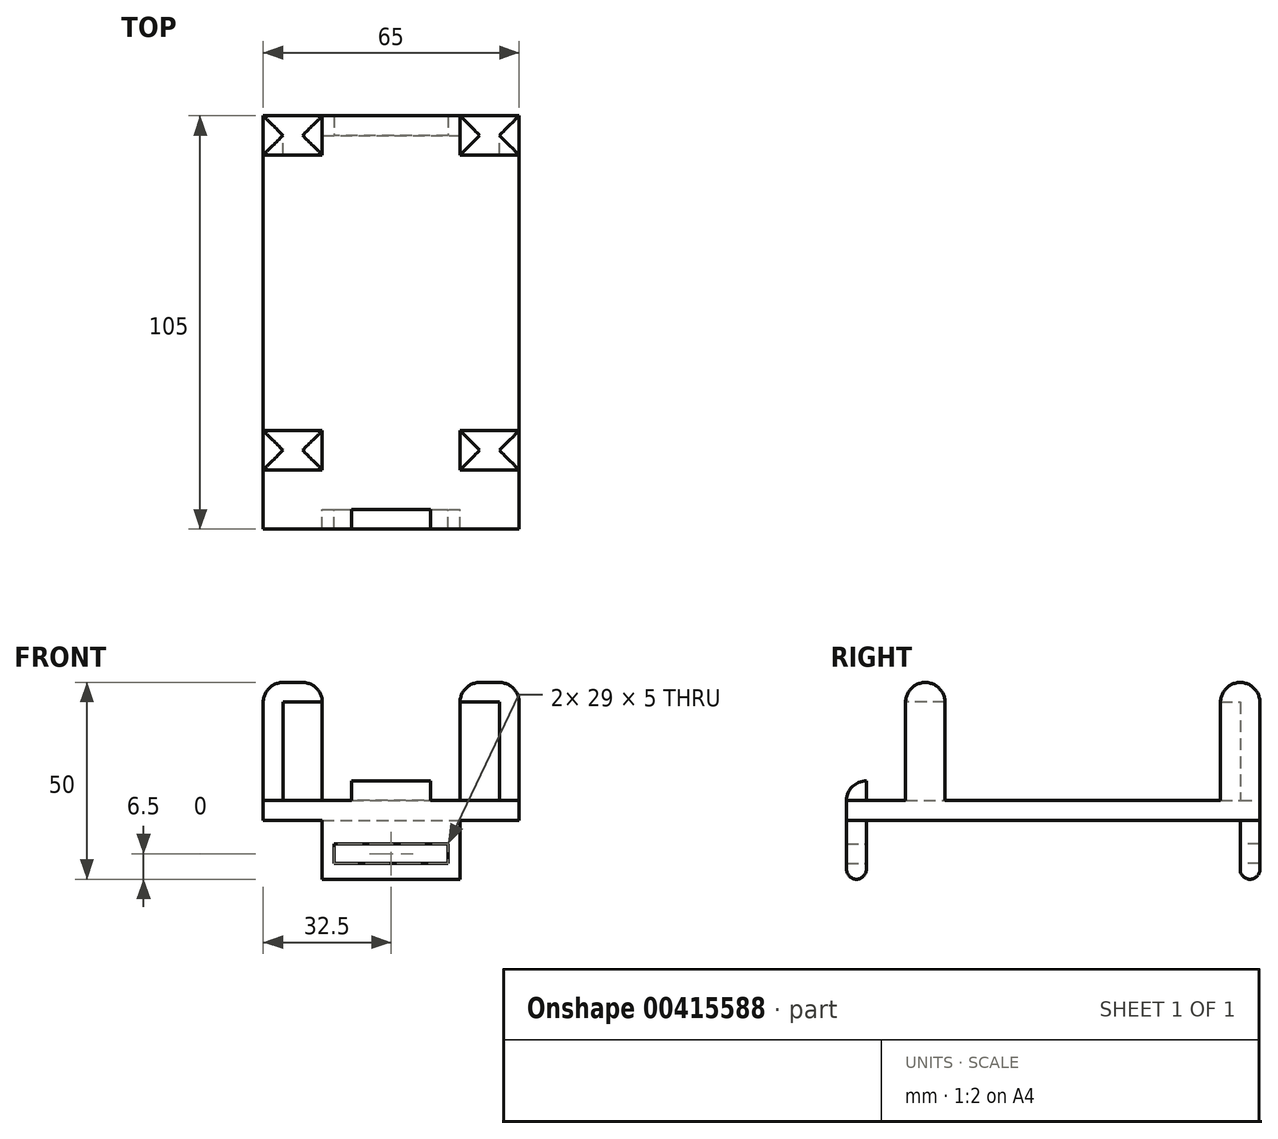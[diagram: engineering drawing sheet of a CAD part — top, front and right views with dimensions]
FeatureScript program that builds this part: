
annotation { "Feature Type Name" : "Feature", "Feature Type Description" : "" }
export const myFeature = defineFeature(function(context is Context, id is Id, definition is map)
    precondition{}
    {
        {
            var Q0;
            Q0=qCreatedBy(makeId("Top.planeOp"),FACE);
            var sketch = newSketch(context, id + "F0", { "sketchPlane" : qUnion([Q0])});
            skLineSegment(sketch, "E0.bottom", {"start": v(32.5, 52.5) * mm, "end": v(-32.5, 52.5) * mm});
            skLineSegment(sketch, "E0.top", {"start": v(32.5, -52.5) * mm, "end": v(-32.5, -52.5) * mm});
            skLineSegment(sketch, "E0.left", {"start": v(32.5, 52.5) * mm, "end": v(32.5, -52.5) * mm});
            skLineSegment(sketch, "E0.right", {"start": v(-32.5, 52.5) * mm, "end": v(-32.5, -52.5) * mm});
            skPoint(sketch, "E0.middle", {"position": v(0, 0) * mm});
            skSolve(sketch);
        }
        {
            var Q0;
            Q0=makeQuery(id+"F0.imprint","IMPRINT",FACE,{"disambiguationData":[TD([[makeQuery(id+"F0.imprint","IMPRINT",EDGE,{"derivedFrom":sQuery(id+"F0.wireOp",EDGE,"E0.bottom")}),1.0]])]});
            var sketch = newSketch(context, id + "F1", { "sketchPlane" : qUnion([Q0])});
            skLineSegment(sketch, "E1.bottom", {"start": v(-27.5, 52.5) * mm, "end": v(-22.5, 52.5) * mm});
            skLineSegment(sketch, "E1.top", {"start": v(-27.5, 47.5) * mm, "end": v(-22.5, 47.5) * mm});
            skLineSegment(sketch, "E1.right", {"start": v(-22.5, 52.5) * mm, "end": v(-22.5, 47.5) * mm});
            skLineSegment(sketch, "E2.MirrorCS", {"start": v(22.5, 52.5) * mm, "end": v(22.5, 47.5) * mm});
            skLineSegment(sketch, "E3.MirrorCS", {"start": v(27.5, 52.5) * mm, "end": v(22.5, 52.5) * mm});
            skLineSegment(sketch, "E4.MirrorCS", {"start": v(27.5, 47.5) * mm, "end": v(22.5, 47.5) * mm});
            skLineSegment(sketch, "E5.top", {"start": v(-27.5, 42.5) * mm, "end": v(-32.5, 42.5) * mm});
            skLineSegment(sketch, "E5.left", {"start": v(-27.5, 47.5) * mm, "end": v(-27.5, 42.5) * mm});
            skLineSegment(sketch, "E5.right", {"start": v(-32.5, 47.5) * mm, "end": v(-32.5, 42.5) * mm});
            skLineSegment(sketch, "E6.MirrorCS", {"start": v(27.5, 47.5) * mm, "end": v(27.5, 42.5) * mm});
            skLineSegment(sketch, "E7.MirrorCS", {"start": v(27.5, 42.5) * mm, "end": v(32.5, 42.5) * mm});
            skLineSegment(sketch, "E8", {"start": v(-32.5, 47.5) * mm, "end": v(-32.5, 52.5) * mm});
            skLineSegment(sketch, "E9", {"start": v(-32.5, 52.5) * mm, "end": v(-27.5, 52.5) * mm});
            skLineSegment(sketch, "E10", {"start": v(32.5, 42.5) * mm, "end": v(32.5, 52.5) * mm});
            skLineSegment(sketch, "E11", {"start": v(32.5, 52.5) * mm, "end": v(27.5, 52.5) * mm});
            skSolve(sketch);
        }
        {
            var Q0;
            Q0=makeQuery(id+"F0.imprint","IMPRINT",FACE,{"disambiguationData":[TD([[makeQuery(id+"F0.imprint","IMPRINT",EDGE,{"derivedFrom":sQuery(id+"F0.wireOp",EDGE,"E0.bottom")}),1.0]])]});
            extrude(context, id + "F2", {"entities" : qUnion([Q0]), "depth" : 5 * mm});
        }
        {
            var Q0;
            Q0=makeQuery(id+"F1.imprint","IMPRINT",FACE,{"disambiguationData":[TD([[makeQuery(id+"F1.imprint","IMPRINT",EDGE,{"derivedFrom":sQuery(id+"F1.wireOp",EDGE,"E1.bottom")}),1.0]])]});
            var Q1;
            Q1=makeQuery(id+"F1.imprint","IMPRINT",FACE,{"disambiguationData":[TD([[makeQuery(id+"F1.imprint","IMPRINT",EDGE,{"derivedFrom":sQuery(id+"F1.wireOp",EDGE,"E2.MirrorCS")}),1.0]])]});
            extrude(context, id + "F3", {"entities" : qUnion([Q0, Q1]), "operationType" : NewBodyOperationType.ADD, "depth" : 35 * mm});
        }
        {
            var Q0;
            Q0=makeQuery(id+"F3.opExtrude","SWEPT_FACE",FACE,{"disambiguationData":[OSD([sQuery(id+"F1.wireOp",EDGE,"E6.MirrorCS")])]});
            var sketch = newSketch(context, id + "F4", { "sketchPlane" : qUnion([Q0])});
            skLineSegment(sketch, "E12.bottom", {"start": v(-42.5, 35) * mm, "end": v(-47.5, 35) * mm});
            skLineSegment(sketch, "E12.top", {"start": v(-42.5, 30) * mm, "end": v(-47.5, 30) * mm});
            skLineSegment(sketch, "E12.left", {"start": v(-42.5, 35) * mm, "end": v(-42.5, 30) * mm});
            skLineSegment(sketch, "E12.right", {"start": v(-47.5, 35) * mm, "end": v(-47.5, 30) * mm});
            skSolve(sketch);
        }
        {
            var Q0;
            Q0=makeQuery(id+"F4.imprint","IMPRINT",FACE,{"disambiguationData":[TD([[makeQuery(id+"F4.imprint","IMPRINT",EDGE,{"derivedFrom":sQuery(id+"F4.wireOp",EDGE,"E12.bottom")}),-1.0]])]});
            extrude(context, id + "F5", {"entities" : qUnion([Q0]), "operationType" : NewBodyOperationType.ADD, "depth" : 5 * mm});
        }
        {
            var Q0;
            Q0=makeQuery(id+"F3.opExtrude","SWEPT_FACE",FACE,{"disambiguationData":[OSD([sQuery(id+"F1.wireOp",EDGE,"E5.left")])]});
            var sketch = newSketch(context, id + "F6", { "sketchPlane" : qUnion([Q0])});
            skLineSegment(sketch, "E13.bottom", {"start": v(42.5, 35) * mm, "end": v(47.5, 35) * mm});
            skLineSegment(sketch, "E13.top", {"start": v(42.5, 30) * mm, "end": v(47.5, 30) * mm});
            skLineSegment(sketch, "E13.left", {"start": v(42.5, 35) * mm, "end": v(42.5, 30) * mm});
            skLineSegment(sketch, "E13.right", {"start": v(47.5, 35) * mm, "end": v(47.5, 30) * mm});
            skSolve(sketch);
        }
        {
            var Q0;
            Q0=makeQuery(id+"F6.imprint","IMPRINT",FACE,{"disambiguationData":[TD([[makeQuery(id+"F6.imprint","IMPRINT",EDGE,{"derivedFrom":sQuery(id+"F6.wireOp",EDGE,"E13.bottom")}),1.0]])]});
            extrude(context, id + "F7", {"entities" : qUnion([Q0]), "operationType" : NewBodyOperationType.ADD, "depth" : 5 * mm});
        }
        {
            var Q0;
            Q0=makeQuery(id+"F2.opExtrude","CAP_FACE",FACE,{"disambiguationData":[OSD([sQuery(id+"F0.wireOp",EDGE,"E0.bottom"),sQuery(id+"F0.wireOp",EDGE,"E0.top"),sQuery(id+"F0.wireOp",EDGE,"E0.left"),sQuery(id+"F0.wireOp",EDGE,"E0.right")])],"isStart":false});
            var sketch = newSketch(context, id + "F8", { "sketchPlane" : qUnion([Q0])});
            skLineSegment(sketch, "E14.bottom", {"start": v(-32.5, -37.5) * mm, "end": v(-27.5, -37.5) * mm});
            skLineSegment(sketch, "E14.top", {"start": v(-32.5, -27.5) * mm, "end": v(-27.5, -27.5) * mm});
            skLineSegment(sketch, "E14.left", {"start": v(-32.5, -37.5) * mm, "end": v(-32.5, -27.5) * mm});
            skLineSegment(sketch, "E14.right", {"start": v(-27.5, -37.5) * mm, "end": v(-27.5, -27.5) * mm});
            skLineSegment(sketch, "E15.MirrorCS", {"start": v(27.5, -37.5) * mm, "end": v(27.5, -27.5) * mm});
            skLineSegment(sketch, "E16.MirrorCS", {"start": v(32.5, -27.5) * mm, "end": v(27.5, -27.5) * mm});
            skLineSegment(sketch, "E17.MirrorCS", {"start": v(32.5, -37.5) * mm, "end": v(27.5, -37.5) * mm});
            skLineSegment(sketch, "E18.MirrorCS", {"start": v(32.5, -37.5) * mm, "end": v(32.5, -27.5) * mm});
            skSolve(sketch);
        }
        {
            var Q0;
            Q0=makeQuery(id+"F8.imprint","IMPRINT",FACE,{"disambiguationData":[TD([[makeQuery(id+"F8.imprint","IMPRINT",EDGE,{"derivedFrom":sQuery(id+"F8.wireOp",EDGE,"E15.MirrorCS")}),-1.0]])]});
            var Q1;
            Q1=makeQuery(id+"F8.imprint","IMPRINT",FACE,{"disambiguationData":[TD([[makeQuery(id+"F8.imprint","IMPRINT",EDGE,{"derivedFrom":sQuery(id+"F8.wireOp",EDGE,"E14.bottom")}),1.0]])]});
            extrude(context, id + "F9", {"entities" : qUnion([Q0, Q1]), "operationType" : NewBodyOperationType.ADD, "depth" : 30 * mm});
        }
        {
            var Q0;
            Q0=makeQuery(id+"F9.opExtrude","SWEPT_FACE",FACE,{"disambiguationData":[OSD([sQuery(id+"F8.wireOp",EDGE,"E14.right")])]});
            var sketch = newSketch(context, id + "F10", { "sketchPlane" : qUnion([Q0])});
            skLineSegment(sketch, "E19.bottom", {"start": v(-27.5, 35) * mm, "end": v(-37.5, 35) * mm});
            skLineSegment(sketch, "E19.top", {"start": v(-27.5, 30) * mm, "end": v(-37.5, 30) * mm});
            skLineSegment(sketch, "E19.left", {"start": v(-27.5, 35) * mm, "end": v(-27.5, 30) * mm});
            skLineSegment(sketch, "E19.right", {"start": v(-37.5, 35) * mm, "end": v(-37.5, 30) * mm});
            skSolve(sketch);
        }
        {
            var Q0;
            Q0=makeQuery(id+"F9.opExtrude","SWEPT_FACE",FACE,{"disambiguationData":[OSD([sQuery(id+"F8.wireOp",EDGE,"E15.MirrorCS")])]});
            var sketch = newSketch(context, id + "F11", { "sketchPlane" : qUnion([Q0])});
            skLineSegment(sketch, "E20.bottom", {"start": v(27.5, 35) * mm, "end": v(37.5, 35) * mm});
            skLineSegment(sketch, "E20.top", {"start": v(27.5, 30) * mm, "end": v(37.5, 30) * mm});
            skLineSegment(sketch, "E20.left", {"start": v(27.5, 35) * mm, "end": v(27.5, 30) * mm});
            skLineSegment(sketch, "E20.right", {"start": v(37.5, 35) * mm, "end": v(37.5, 30) * mm});
            skSolve(sketch);
        }
        {
            var Q0;
            Q0 = qSketchRegion(id + "F11", true);
            extrude(context, id + "F12", {"entities" : qUnion([Q0]), "operationType" : NewBodyOperationType.ADD, "depth" : 10 * mm});
        }
        {
            var Q0;
            Q0=makeQuery(id+"F10.imprint","IMPRINT",FACE,{"disambiguationData":[TD([[makeQuery(id+"F10.imprint","IMPRINT",EDGE,{"derivedFrom":sQuery(id+"F10.wireOp",EDGE,"E19.bottom")}),-1.0]])]});
            extrude(context, id + "F13", {"entities" : qUnion([Q0]), "operationType" : NewBodyOperationType.ADD, "depth" : 10 * mm});
        }
        {
            var Q0;
            Q0=makeQuery(id+"F5.boolean.opBoolean","MERGE",FACE,{"derivedFrom":[makeQuery(id+"F3.opExtrude","SWEPT_FACE",FACE,{"disambiguationData":[OSD([sQuery(id+"F1.wireOp",EDGE,"E2.MirrorCS")])]}),makeQuery(id+"F5.opExtrude","CAP_FACE",FACE,{"disambiguationData":[OSD([sQuery(id+"F4.wireOp",EDGE,"E12.bottom"),sQuery(id+"F4.wireOp",EDGE,"E12.top"),sQuery(id+"F4.wireOp",EDGE,"E12.left"),sQuery(id+"F4.wireOp",EDGE,"E12.right")])],"isStart":false})]});
            extrude(context, id + "F14", {"entities" : qUnion([Q0]), "operationType" : NewBodyOperationType.ADD, "depth" : 5 * mm});
        }
        {
            var Q0;
            Q0=makeQuery(id+"F7.boolean.opBoolean","MERGE",FACE,{"derivedFrom":[makeQuery(id+"F3.opExtrude","SWEPT_FACE",FACE,{"disambiguationData":[OSD([sQuery(id+"F1.wireOp",EDGE,"E1.right")])]}),makeQuery(id+"F7.opExtrude","CAP_FACE",FACE,{"disambiguationData":[OSD([sQuery(id+"F6.wireOp",EDGE,"E13.bottom"),sQuery(id+"F6.wireOp",EDGE,"E13.top"),sQuery(id+"F6.wireOp",EDGE,"E13.left"),sQuery(id+"F6.wireOp",EDGE,"E13.right")])],"isStart":false})]});
            extrude(context, id + "F15", {"entities" : qUnion([Q0]), "operationType" : NewBodyOperationType.ADD, "depth" : 5 * mm});
        }
        {
            var Q0;
            Q0=makeQuery(id+"F2.opExtrude","CAP_FACE",FACE,{"disambiguationData":[OSD([sQuery(id+"F0.wireOp",EDGE,"E0.bottom"),sQuery(id+"F0.wireOp",EDGE,"E0.top"),sQuery(id+"F0.wireOp",EDGE,"E0.left"),sQuery(id+"F0.wireOp",EDGE,"E0.right")])],"isStart":false});
            var sketch = newSketch(context, id + "F16", { "sketchPlane" : qUnion([Q0])});
            skLineSegment(sketch, "E21.bottom", {"start": v(-10, -52.5) * mm, "end": v(10, -52.5) * mm});
            skLineSegment(sketch, "E21.top", {"start": v(-10, -47.5) * mm, "end": v(10, -47.5) * mm});
            skLineSegment(sketch, "E21.left", {"start": v(-10, -52.5) * mm, "end": v(-10, -47.5) * mm});
            skLineSegment(sketch, "E21.right", {"start": v(10, -52.5) * mm, "end": v(10, -47.5) * mm});
            skSolve(sketch);
        }
        {
            var Q0;
            Q0=makeQuery(id+"F16.imprint","IMPRINT",FACE,{"disambiguationData":[TD([[makeQuery(id+"F16.imprint","IMPRINT",EDGE,{"derivedFrom":sQuery(id+"F16.wireOp",EDGE,"E21.bottom")}),-1.0]])]});
            extrude(context, id + "F17", {"entities" : qUnion([Q0]), "operationType" : NewBodyOperationType.ADD, "depth" : 5 * mm});
        }
        {
            var Q0;
            Q0=makeQuery(id+"F2.opExtrude","CAP_FACE",FACE,{"disambiguationData":[OSD([sQuery(id+"F0.wireOp",EDGE,"E0.bottom"),sQuery(id+"F0.wireOp",EDGE,"E0.top"),sQuery(id+"F0.wireOp",EDGE,"E0.left"),sQuery(id+"F0.wireOp",EDGE,"E0.right")])],"isStart":true});
            var sketch = newSketch(context, id + "F18", { "sketchPlane" : qUnion([Q0])});
            skLineSegment(sketch, "E22.bottom", {"start": v(-17.5, 52.5) * mm, "end": v(17.5, 52.5) * mm});
            skLineSegment(sketch, "E22.top", {"start": v(-17.5, 47.5) * mm, "end": v(17.5, 47.5) * mm});
            skLineSegment(sketch, "E22.left", {"start": v(-17.5, 52.5) * mm, "end": v(-17.5, 47.5) * mm});
            skLineSegment(sketch, "E22.right", {"start": v(17.5, 52.5) * mm, "end": v(17.5, 47.5) * mm});
            skLineSegment(sketch, "E23.MirrorCS", {"start": v(-17.5, -47.5) * mm, "end": v(17.5, -47.5) * mm});
            skLineSegment(sketch, "E24.MirrorCS", {"start": v(-17.5, -52.5) * mm, "end": v(17.5, -52.5) * mm});
            skLineSegment(sketch, "E25.MirrorCS", {"start": v(17.5, -52.5) * mm, "end": v(17.5, -47.5) * mm});
            skLineSegment(sketch, "E26.MirrorCS", {"start": v(-17.5, -52.5) * mm, "end": v(-17.5, -47.5) * mm});
            skSolve(sketch);
        }
        {
            var Q0;
            Q0 = qSketchRegion(id + "F18", true);
            extrude(context, id + "F19", {"entities" : qUnion([Q0]), "operationType" : NewBodyOperationType.ADD, "depth" : 15 * mm});
        }
        {
            var Q0;
            Q0=makeQuery(id+"F19.opExtrude","SWEPT_FACE",FACE,{"disambiguationData":[OSD([sQuery(id+"F18.wireOp",EDGE,"E22.top")])]});
            var sketch = newSketch(context, id + "F20", { "sketchPlane" : qUnion([Q0])});
            skLineSegment(sketch, "E27.bottom", {"start": v(14.5, -11) * mm, "end": v(-14.5, -11) * mm});
            skLineSegment(sketch, "E27.top", {"start": v(14.5, -6) * mm, "end": v(-14.5, -6) * mm});
            skLineSegment(sketch, "E27.left", {"start": v(14.5, -11) * mm, "end": v(14.5, -6) * mm});
            skLineSegment(sketch, "E27.right", {"start": v(-14.5, -11) * mm, "end": v(-14.5, -6) * mm});
            skSolve(sketch);
        }
        {
            var Q0;
            Q0=makeQuery(id+"F19.opExtrude","SWEPT_FACE",FACE,{"disambiguationData":[OSD([sQuery(id+"F18.wireOp",EDGE,"E23.MirrorCS")])]});
            var sketch = newSketch(context, id + "F21", { "sketchPlane" : qUnion([Q0])});
            skLineSegment(sketch, "E28.bottom", {"start": v(14.5, -11) * mm, "end": v(-14.5, -11) * mm});
            skLineSegment(sketch, "E28.top", {"start": v(14.5, -6) * mm, "end": v(-14.5, -6) * mm});
            skLineSegment(sketch, "E28.left", {"start": v(14.5, -11) * mm, "end": v(14.5, -6) * mm});
            skLineSegment(sketch, "E28.right", {"start": v(-14.5, -11) * mm, "end": v(-14.5, -6) * mm});
            skSolve(sketch);
        }
        {
            var Q0;
            Q0=makeQuery(id+"F21.imprint","IMPRINT",FACE,{"disambiguationData":[TD([[makeQuery(id+"F21.imprint","IMPRINT",EDGE,{"derivedFrom":sQuery(id+"F21.wireOp",EDGE,"E28.bottom")}),-1.0]])]});
            extrude(context, id + "F22", {"entities" : qUnion([Q0]), "operationType" : NewBodyOperationType.REMOVE, "oppositeDirection" : true, "depth" : 25 * mm});
        }
        {
            var Q0;
            Q0=makeQuery(id+"F20.imprint","IMPRINT",FACE,{"disambiguationData":[TD([[makeQuery(id+"F20.imprint","IMPRINT",EDGE,{"derivedFrom":sQuery(id+"F20.wireOp",EDGE,"E27.bottom")}),-1.0]])]});
            extrude(context, id + "F23", {"entities" : qUnion([Q0]), "operationType" : NewBodyOperationType.REMOVE, "oppositeDirection" : true, "depth" : 25 * mm});
        }
        {
            var Q0;
            Q0=makeQuery(id+"F19.opExtrude","CAP_EDGE",EDGE,{"disambiguationData":[OSD([sQuery(id+"F18.wireOp",EDGE,"E24.MirrorCS")])],"isStart":false});
            var Q1;
            Q1=makeQuery(id+"F19.opExtrude","CAP_EDGE",EDGE,{"disambiguationData":[OSD([sQuery(id+"F18.wireOp",EDGE,"E23.MirrorCS")])],"isStart":false});
            var Q2;
            Q2=makeQuery(id+"F19.opExtrude","CAP_EDGE",EDGE,{"disambiguationData":[OSD([sQuery(id+"F18.wireOp",EDGE,"E22.bottom")])],"isStart":false});
            var Q3;
            Q3=makeQuery(id+"F19.opExtrude","CAP_EDGE",EDGE,{"disambiguationData":[OSD([sQuery(id+"F18.wireOp",EDGE,"E22.top")])],"isStart":false});
            fillet(context, id + "F24", {"entities" : qUnion([Q0, Q1, Q2, Q3]), "radius" : 2.5 * mm, "tangentPropagation" : true, "allowEdgeOverflow" : false});
        }
        {
            var Q0;
            Q0=makeQuery(id+"F9.opExtrude","CAP_EDGE",EDGE,{"disambiguationData":[OSD([sQuery(id+"F8.wireOp",EDGE,"E14.left")])],"isStart":false});
            var Q1;
            Q1=makeQuery(id+"F9.opExtrude","CAP_EDGE",EDGE,{"disambiguationData":[OSD([sQuery(id+"F8.wireOp",EDGE,"E18.MirrorCS")])],"isStart":false});
            var Q2;
            Q2=makeQuery(id+"F12.opExtrude","CAP_EDGE",EDGE,{"disambiguationData":[OSD([sQuery(id+"F11.wireOp",EDGE,"E20.bottom")])],"isStart":false});
            var Q3;
            Q3=makeQuery(id+"F13.opExtrude","CAP_EDGE",EDGE,{"disambiguationData":[OSD([sQuery(id+"F10.wireOp",EDGE,"E19.bottom")])],"isStart":false});
            var Q4;
            {var subQ0=sQuery(id+"F1.wireOp",EDGE,"E1.bottom");Q4=makeQuery(id+"F15.boolean.opBoolean","MERGE",EDGE,{"derivedFrom":[makeQuery(id+"F3.opExtrude","CAP_EDGE",EDGE,{"disambiguationData":[OSD([subQ0,sQuery(id+"F1.wireOp",EDGE,"E9")])],"isStart":false}),makeQuery(id+"F15.opExtrude","SWEPT_EDGE",EDGE,{"disambiguationData":[OSD([sQuery(id+"F0.wireOp",EDGE,"E0.bottom"),subQ0,sQuery(id+"F1.wireOp",EDGE,"E1.right")])]})]});}
            var Q5;
            {var subQ0=sQuery(id+"F1.wireOp",EDGE,"E3.MirrorCS");Q5=makeQuery(id+"F14.boolean.opBoolean","MERGE",EDGE,{"derivedFrom":[makeQuery(id+"F3.opExtrude","CAP_EDGE",EDGE,{"disambiguationData":[OSD([subQ0,sQuery(id+"F1.wireOp",EDGE,"E11")])],"isStart":false}),makeQuery(id+"F14.opExtrude","SWEPT_EDGE",EDGE,{"disambiguationData":[OSD([sQuery(id+"F0.wireOp",EDGE,"E0.bottom"),sQuery(id+"F1.wireOp",EDGE,"E2.MirrorCS"),subQ0])]})]});}
            var Q6;
            Q6=makeQuery(id+"F3.opExtrude","CAP_EDGE",EDGE,{"disambiguationData":[OSD([sQuery(id+"F1.wireOp",EDGE,"E10")])],"isStart":false});
            var Q7;
            {var subQ0=sQuery(id+"F4.wireOp",EDGE,"E12.left");var subQ1=sQuery(id+"F4.wireOp",EDGE,"E12.bottom");Q7=makeQuery(id+"F14.boolean.opBoolean","MERGE",EDGE,{"derivedFrom":[makeQuery(id+"F5.boolean.opBoolean","MERGE",EDGE,{"derivedFrom":[makeQuery(id+"F3.opExtrude","CAP_EDGE",EDGE,{"disambiguationData":[OSD([sQuery(id+"F1.wireOp",EDGE,"E7.MirrorCS")])],"isStart":false}),makeQuery(id+"F5.opExtrude","SWEPT_EDGE",EDGE,{"disambiguationData":[OSD([subQ1,subQ0])]})]}),makeQuery(id+"F14.opExtrude","SWEPT_EDGE",EDGE,{"disambiguationData":[OSD([subQ1,subQ0])]})]});}
            var Q8;
            Q8=makeQuery(id+"F14.opExtrude","CAP_EDGE",EDGE,{"disambiguationData":[OSD([sQuery(id+"F1.wireOp",EDGE,"E2.MirrorCS"),sQuery(id+"F4.wireOp",EDGE,"E12.bottom")])],"isStart":false});
            var Q9;
            {var subQ0=sQuery(id+"F6.wireOp",EDGE,"E13.left");var subQ1=sQuery(id+"F6.wireOp",EDGE,"E13.bottom");Q9=makeQuery(id+"F15.boolean.opBoolean","MERGE",EDGE,{"derivedFrom":[makeQuery(id+"F7.boolean.opBoolean","MERGE",EDGE,{"derivedFrom":[makeQuery(id+"F3.opExtrude","CAP_EDGE",EDGE,{"disambiguationData":[OSD([sQuery(id+"F1.wireOp",EDGE,"E5.top")])],"isStart":false}),makeQuery(id+"F7.opExtrude","SWEPT_EDGE",EDGE,{"disambiguationData":[OSD([subQ1,subQ0])]})]}),makeQuery(id+"F15.opExtrude","SWEPT_EDGE",EDGE,{"disambiguationData":[OSD([subQ1,subQ0])]})]});}
            var Q10;
            Q10=makeQuery(id+"F15.opExtrude","CAP_EDGE",EDGE,{"disambiguationData":[OSD([sQuery(id+"F1.wireOp",EDGE,"E1.right"),sQuery(id+"F6.wireOp",EDGE,"E13.bottom")])],"isStart":false});
            var Q11;
            Q11=makeQuery(id+"F3.opExtrude","CAP_EDGE",EDGE,{"disambiguationData":[OSD([sQuery(id+"F1.wireOp",EDGE,"E5.right"),sQuery(id+"F1.wireOp",EDGE,"E8")])],"isStart":false});
            var Q12;
            Q12=makeQuery(id+"F13.boolean.opBoolean","MERGE",EDGE,{"derivedFrom":[makeQuery(id+"F9.opExtrude","CAP_EDGE",EDGE,{"disambiguationData":[OSD([sQuery(id+"F8.wireOp",EDGE,"E14.bottom")])],"isStart":false}),makeQuery(id+"F13.opExtrude","SWEPT_EDGE",EDGE,{"disambiguationData":[OSD([sQuery(id+"F10.wireOp",EDGE,"E19.bottom"),sQuery(id+"F10.wireOp",EDGE,"E19.right")])]})]});
            var Q13;
            Q13=makeQuery(id+"F13.boolean.opBoolean","MERGE",EDGE,{"derivedFrom":[makeQuery(id+"F9.opExtrude","CAP_EDGE",EDGE,{"disambiguationData":[OSD([sQuery(id+"F8.wireOp",EDGE,"E14.top")])],"isStart":false}),makeQuery(id+"F13.opExtrude","SWEPT_EDGE",EDGE,{"disambiguationData":[OSD([sQuery(id+"F10.wireOp",EDGE,"E19.bottom"),sQuery(id+"F10.wireOp",EDGE,"E19.left")])]})]});
            var Q14;
            Q14=makeQuery(id+"F12.boolean.opBoolean","MERGE",EDGE,{"derivedFrom":[makeQuery(id+"F9.opExtrude","CAP_EDGE",EDGE,{"disambiguationData":[OSD([sQuery(id+"F8.wireOp",EDGE,"E17.MirrorCS")])],"isStart":false}),makeQuery(id+"F12.opExtrude","SWEPT_EDGE",EDGE,{"disambiguationData":[OSD([sQuery(id+"F11.wireOp",EDGE,"E20.bottom"),sQuery(id+"F11.wireOp",EDGE,"E20.right")])]})]});
            var Q15;
            Q15=makeQuery(id+"F12.boolean.opBoolean","MERGE",EDGE,{"derivedFrom":[makeQuery(id+"F9.opExtrude","CAP_EDGE",EDGE,{"disambiguationData":[OSD([sQuery(id+"F8.wireOp",EDGE,"E16.MirrorCS")])],"isStart":false}),makeQuery(id+"F12.opExtrude","SWEPT_EDGE",EDGE,{"disambiguationData":[OSD([sQuery(id+"F11.wireOp",EDGE,"E20.bottom"),sQuery(id+"F11.wireOp",EDGE,"E20.left")])]})]});
            var Q16;
            Q16=makeQuery(id+"F17.opExtrude","CAP_EDGE",EDGE,{"disambiguationData":[OSD([sQuery(id+"F16.wireOp",EDGE,"E21.bottom")])],"isStart":false});
            fillet(context, id + "F25", {"entities" : qUnion([Q0, Q1, Q2, Q3, Q4, Q5, Q6, Q7, Q8, Q9, Q10, Q11, Q12, Q13, Q14, Q15, Q16]), "radius" : 5 * mm, "tangentPropagation" : true, "allowEdgeOverflow" : false});
        }
    });
